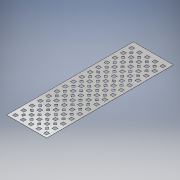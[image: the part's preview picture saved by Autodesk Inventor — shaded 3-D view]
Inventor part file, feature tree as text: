
AUTODESK INVENTOR PART (.ipt)
format: ipt  version: 2018 (Build 220112000, 112)  size: 626,688 bytes
history: native  units: in
note: dims shown in document units (in); Inventor stores cm internally (conversion verified against a paired STEP export)
features: extrude x2, sketch x2
ambient origin geometry x8: Origin, YZ Plane, XZ Plane, XY Plane, X Axis, Y Axis, Z Axis, Center Point
bodies: Solid1 (feature_tree)
feature tree (4):
  extrude  "Extrusion1"  Depth=7.48in
  extrude  "Extrusion2"  Depth=0.18in
  sketch  "Sketch1"  dims[d0=2.362in d1=7.48in]
  sketch  "Sketch2"  dims[d2=0.01in d3=0.0in d4=0.18in d5=0.18in d6=0.3937in d8=1.0in d9=1.9685in d11=0.46in d13=0.3937in d15=1.0in d16=5.9055in d18=0.49in d20=0.14in d21=0.14in d22=0.01in d23=0.0in]
